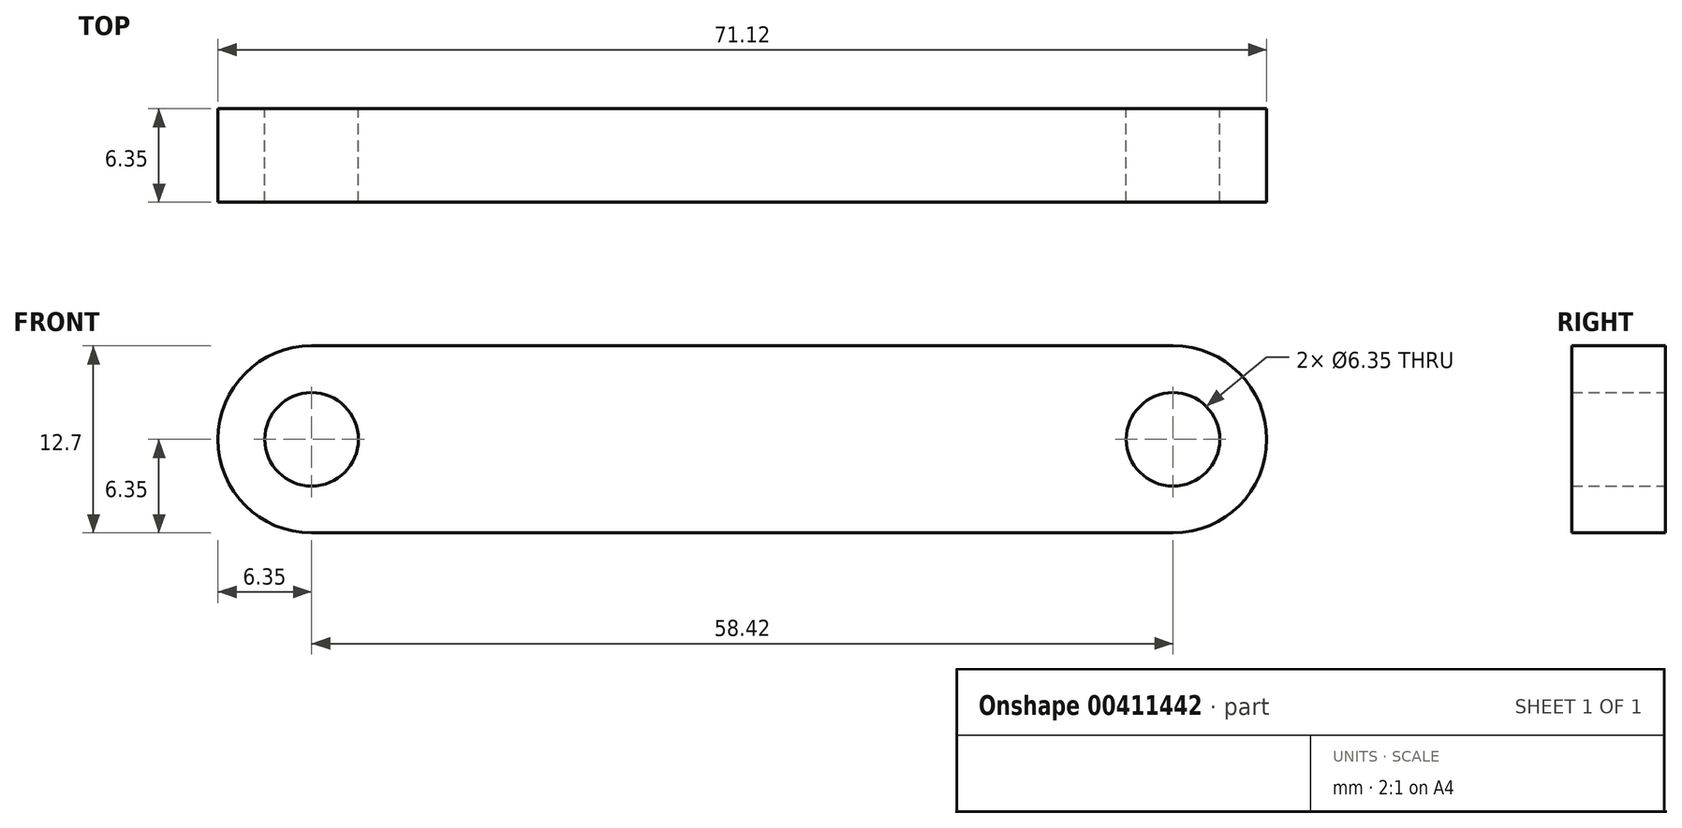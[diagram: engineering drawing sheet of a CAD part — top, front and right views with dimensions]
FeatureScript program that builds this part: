
annotation { "Feature Type Name" : "Feature", "Feature Type Description" : "" }
export const myFeature = defineFeature(function(context is Context, id is Id, definition is map)
    precondition{}
    {
        {
            var Q0;
            Q0=qCreatedBy(makeId("Front.planeOp"),FACE);
            var sketch = newSketch(context, id + "F0", { "sketchPlane" : qUnion([Q0])});
            skArc(sketch, "E0", {"start": v(0, 6.35) * mm, "mid": v(-6.35, 0) * mm, "end": v(0, -6.35) * mm});
            skLineSegment(sketch, "E1.bottom", {"start": v(0, 6.35) * mm, "end": v(58.42, 6.35) * mm});
            skLineSegment(sketch, "E1.top", {"start": v(0, -6.35) * mm, "end": v(58.42, -6.35) * mm});
            skArc(sketch, "E2", {"start": v(58.42, -6.35) * mm, "mid": v(64.77, 0) * mm, "end": v(58.42, 6.35) * mm});
            skCircle(sketch, "E3", {"center": v(0, 0) * mm, "radius": 3.18 * mm});
            skCircle(sketch, "E4", {"center": v(58.42, 0) * mm, "radius": 3.18 * mm});
            skSolve(sketch);
        }
        {
            var Q0;
            Q0 = qSketchRegion(id + "F0", true);
            extrude(context, id + "F1", {"entities" : qUnion([Q0]), "depth" : 6.35 * mm});
        }
    });
